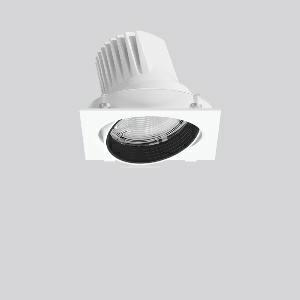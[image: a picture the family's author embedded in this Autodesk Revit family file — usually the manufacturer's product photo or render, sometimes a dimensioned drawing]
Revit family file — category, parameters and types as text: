
# Revit family: magcardo_maxi_722190_002_2_76_31cd
name_source: partatom
category: Lighting Fixtures
units: mm (PartAtom-declared; Revit-internal decimal feet)

## family parameters
Cut with Voids When Loaded = No
Host = Face
Light Source = No
Part Type = Normal
Room Calculation Point = No
Round Connector Dimension = Use Diameter
Shared = No

## types (1)
- MAGCARDO maxi (1 x LED Modul 927, 2650 lm, 2700)
    Apparent Load = 25 VA
    Approval mark = CE
    CIE Flux Codes = 97 100 100 100 100
    Color Rendering = 92
    Color Temperature = 2700
    Default Elevation = 1800 mm
    Description = Series: MAGCARDO maxi
Projector unit for tool-free mounting in separate recessed frame. Luminaire top: die-cast aluminium, powder-coated. Rotation range 356° and swivel range ± 35°. Inner cover prevents view into the false ceiling. Black plastic ring and recessed LED to prevent glare from the side. Optical assembly with lens made of plastic (polycarbonate) for the best homogeneous light distribution - can be changed without tools. Best colour rendering index Ra>90. Magnetic click locking mechanism for quick and convenient installation without tools: insert the recessed frame (1, 2 or 3-lamp) with clamp fastener (no tools required), push the luminaire head with the base plate into the recessed frame and fix magnetically. Including separate LED converter with connecting cable 600 mm.High quality converter without flickering and stroboscopic effect. Through-wiring box (5 pole) available as accessory. The following accessories can be mounted without use of tools: interchangeable lenses, honeycomb louvre, clear and frosted diffusers, white interchangeable plastic ring.Modular design: recessed mounting frame must be ordered separately! 
Colour: traffic white, matt (RAL 9016)
Length: 172 mm
Width: 167 mm
Height: 137 mm
Recess height: 155 mm
Lamp: LED
Socket: without socket
Colour temperature: 2700K
Colour rendering index (CRI): 92
System power: 25 W
Rated luminous flux: 2650 lm
Luminous efficiency: 106 lm/W
Control gear: Converter, dimmable, DALI
Protection class: II
Type of protection: IP 20
    Height = 0 mm  [stored 0 ft]
    Lamp = 1 x LED Modul 927
    Lamp Light Flux = 2650 lm
    Lamp count = 1
    Length = 172 mm
    Lifetime = 50000 h
    Luminous efficacy = 106 lm/W
    Manufacturer = RZB
    ModVariant = No
    Model = 722190.002.2.76
    Mounting Place = Ceiling, Wall
    Mounting Type = Recessed
    Number of Poles = 1
    OnlyDefault = Yes
    Power Factor = 1
    Product Name = MAGCARDO maxi
    Product group = Recessed projectors
    ProductGroupID = 401
    Protection Class = Protection class II
    Protection Degree = IP 20
    RLX_Detail_Level = 1
    RLX_Emergency_Light_Flux = 0 lm
    RLX_Emergency_Type = 0
    RLX_Emergency_Type_DB = No
    RlxData = <blob elided: 40937 chars, md5=df7567c9>
    Socket = socket
    Standby Power = 0 W
    System Light Flux = 2650 lm
    System Power = 25 W
    Type Comments = Product without accessories
    Type Image = 722048.002.jpg
    URL = http://relux.com
    VarID = ---
    Voltage = 230 V
    Voltage Range = 220-240 V
    Weight = 0.00 kg
    Width = 167 mm

note: [stored X ft] marks values corroborated as IEEE doubles in the binary element streams (Revit-internal decimal feet)

## geometry (parser evidence)
native form markers: Blend x4, Sweep x11
no freeform markers — native parametric forms only
